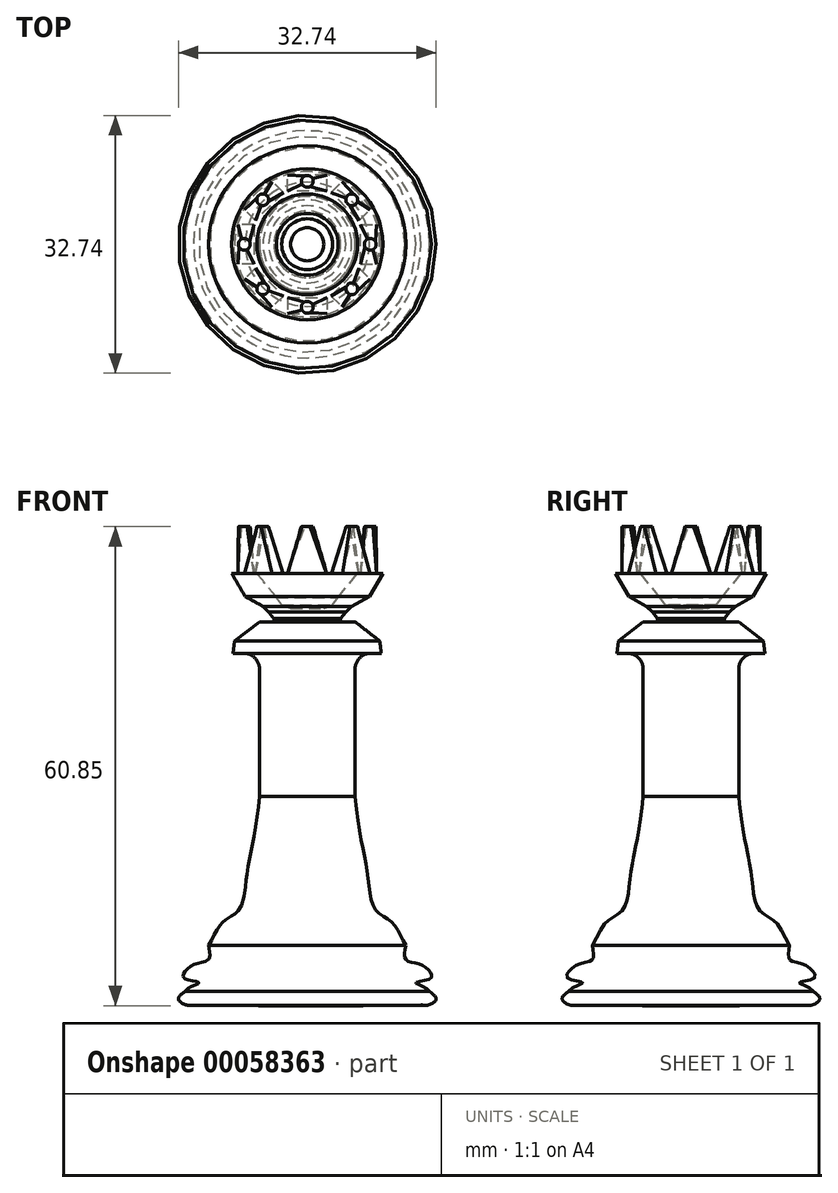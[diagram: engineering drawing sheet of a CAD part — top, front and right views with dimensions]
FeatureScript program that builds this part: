
annotation { "Feature Type Name" : "Feature", "Feature Type Description" : "" }
export const myFeature = defineFeature(function(context is Context, id is Id, definition is map)
    precondition{}
    {
        {
            var Q0;
            Q0=qCreatedBy(makeId("Front.planeOp"),FACE);
            var sketch = newSketch(context, id + "F0", { "sketchPlane" : qUnion([Q0])});
            skLineSegment(sketch, "E0.bottom", {"start": v(0, 26.82) * mm, "end": v(-6.07, 26.82) * mm});
            skLineSegment(sketch, "E0.top", {"start": v(0, -21.95) * mm, "end": v(-6.17, -21.95) * mm});
            skLineSegment(sketch, "E0.left", {"start": v(0, 26.82) * mm, "end": v(0, -21.95) * mm});
            skLineSegment(sketch, "E0.right", {"start": v(-6.07, 26.82) * mm, "end": v(-6.07, 4.6) * mm});
            skLineSegment(sketch, "E1", {"start": v(-6.07, 26.82) * mm, "end": v(-9.2, 24.38) * mm});
            skLineSegment(sketch, "E2", {"start": v(-9.2, 24.38) * mm, "end": v(-9.4, 22.82) * mm});
            skLineSegment(sketch, "E3", {"start": v(-9.4, 22.82) * mm, "end": v(-6.07, 22.82) * mm});
            skLineSegment(sketch, "E4", {"start": v(-6.07, 22.82) * mm, "end": v(-6.07, 26.82) * mm});
            skLineSegment(sketch, "E5", {"start": v(-6.07, -14.27) * mm, "end": v(-6.17, -21.95) * mm});
            skPoint(sketch, "E6.1.internal.snap0", {"position": v(-9.3, -14.27) * mm});
            skPoint(sketch, "E7.1.internal.snap0", {"position": v(-10.85, -21.06) * mm});
            skFitSpline(sketch, "E7", {"points": [v(-12.53, -14.27) * mm, v(-10.85, -11.46) * mm, v(-8.62, -9.7) * mm, v(-7.64, -5) * mm, v(-6.07, 4.6) * mm], "startDerivative": vector(8.85, 12.63) * mm, "endDerivative": vector(3.32, 39) * mm});
            skPoint(sketch, "E8.start.orphan", {"position": v(-15.63, -17.73) * mm});
            skPoint(sketch, "E9.start.orphan", {"position": v(-15.63, -18.5) * mm});
            skPoint(sketch, "E10.orphan", {"position": v(-15.54, -20.16) * mm});
            skFitSpline(sketch, "E11", {"points": [v(-12.53, -14.27) * mm, v(-12.53, -16.09) * mm, v(-14.15, -16.64) * mm, v(-15.63, -17.73) * mm, v(-15.63, -18.5) * mm, v(-13.78, -19.05) * mm, v(-15.54, -20.16) * mm, v(-14.43, -21.36) * mm, v(-12.53, -20.16) * mm, v(-6.17, -21.95) * mm], "startDerivative": vector(4.35, -21.12) * mm, "endDerivative": vector(37.5, -4.8) * mm});
            skLineSegment(sketch, "E12", {"start": v(-6.17, -21.95) * mm, "end": v(-14.43, -21.85) * mm});
            skFitSpline(sketch, "E13", {"points": [v(-14.43, -21.85) * mm, v(-15.44, -21.85) * mm, v(-16.37, -21.08) * mm, v(-15.54, -20.16) * mm], "startDerivative": vector(-3.06, -0.55) * mm, "endDerivative": vector(3.74, 2.62) * mm});
            skSolve(sketch);
        }
        {
            var Q0;
            Q0=qSketchRegion(id+"F0",true);
            var Q1;
            Q1=sQuery(id+"F0.wireOp",EDGE,"E0.left");
            revolve(context, id + "F1", {"entities" : qUnion([Q0]), "axis" : qUnion([Q1]), "revolveType" : RevolveType.FULL});
        }
        {
            var Q0;
            Q0=qCreatedBy(makeId("Front.planeOp"),FACE);
            var sketch = newSketch(context, id + "F2", { "sketchPlane" : qUnion([Q0])});
            skLineSegment(sketch, "E14", {"start": v(0, 26.87) * mm, "end": v(0, 28.51) * mm});
            skLineSegment(sketch, "E15", {"start": v(0, 28.51) * mm, "end": v(-2.1, 28.51) * mm});
            skLineSegment(sketch, "E16", {"start": v(-2.1, 28.51) * mm, "end": v(-3.24, 28.95) * mm});
            skLineSegment(sketch, "E17", {"start": v(-3.24, 28.95) * mm, "end": v(-3.93, 29.92) * mm});
            skLineSegment(sketch, "E18", {"start": v(-3.93, 29.92) * mm, "end": v(-6.4, 32.97) * mm});
            skLineSegment(sketch, "E19", {"start": v(-6.4, 32.97) * mm, "end": v(-9.6, 32.97) * mm});
            skLineSegment(sketch, "E20", {"start": v(-9.6, 32.97) * mm, "end": v(-7.88, 30.03) * mm});
            skLineSegment(sketch, "E21", {"start": v(-7.88, 30.03) * mm, "end": v(-5.64, 28.78) * mm});
            skLineSegment(sketch, "E22", {"start": v(-5.64, 28.78) * mm, "end": v(-4.9, 28.04) * mm});
            skLineSegment(sketch, "E23", {"start": v(-4.9, 28.04) * mm, "end": v(-4.25, 27.2) * mm});
            skLineSegment(sketch, "E24", {"start": v(-4.25, 27.2) * mm, "end": v(-4.25, 26.55) * mm});
            skLineSegment(sketch, "E25", {"start": v(-4.25, 26.55) * mm, "end": v(0, 26.55) * mm});
            skLineSegment(sketch, "E26", {"start": v(0, 26.55) * mm, "end": v(0, 28.51) * mm});
            skSolve(sketch);
        }
        {
            var Q0;
            Q0=qSketchRegion(id+"F2",true);
            var Q1;
            Q1=sQuery(id+"F2.wireOp",EDGE,"E14");
            revolve(context, id + "F3", {"operationType" : NewBodyOperationType.ADD, "entities" : qUnion([Q0]), "axis" : qUnion([Q1]), "revolveType" : RevolveType.FULL});
        }
        {
            var Q0;
            Q0=makeQuery(id+"F1.opRevolve","SWEPT_EDGE",EDGE,{"disambiguationData":[OSD([sQuery(id+"F0.wireOp",EDGE,"E0.right"),sQuery(id+"F0.wireOp",EDGE,"E3"),sQuery(id+"F0.wireOp",EDGE,"E4")])]});
            fillet(context, id + "F4", {"entities" : qUnion([Q0]), "radius" : 2 * mm, "tangentPropagation" : true, "allowEdgeOverflow" : false});
        }
        {
            var Q0;
            Q0=qCreatedBy(makeId("Top.planeOp"),FACE);
            cPlane(context, id + "F5", {"entities" : qUnion([Q0]), "cplaneType" : CPlaneType.OFFSET, "offset" : 32.9 * mm, "width" : 150 * mm, "height" : 150 * mm});
        }
        {
            var Q0;
            Q0=qCreatedBy(id+"F5.planeOp",FACE);
            cPlane(context, id + "F6", {"entities" : qUnion([Q0]), "cplaneType" : CPlaneType.OFFSET, "offset" : 6 * mm, "width" : 150 * mm, "height" : 150 * mm});
        }
        {
            var Q0;
            Q0=qCreatedBy(id+"F5.planeOp",FACE);
            var sketch = newSketch(context, id + "F7", { "sketchPlane" : qUnion([Q0])});
            skLineSegment(sketch, "E27.MirrorCS", {"start": v(2.5, -6.78) * mm, "end": v(2.5, -8.78) * mm});
            skLineSegment(sketch, "E28.MirrorCS", {"start": v(-2.5, -6.78) * mm, "end": v(-2.5, -8.78) * mm});
            skLineSegment(sketch, "E29.MirrorCS", {"start": v(-2.5, -8.78) * mm, "end": v(2.5, -8.78) * mm});
            skLineSegment(sketch, "E30.MirrorCS", {"start": v(-2.5, -6.78) * mm, "end": v(2.5, -6.78) * mm});
            skLineSegment(sketch, "E31", {"start": v(0, 0) * mm, "end": v(0, -8.78) * mm, "construction": true});
            skSolve(sketch);
        }
        {
            var Q0;
            Q0=qCreatedBy(id+"F6.planeOp",FACE);
            var sketch = newSketch(context, id + "F8", { "sketchPlane" : qUnion([Q0])});
            skLineSegment(sketch, "E32", {"start": v(0, 0) * mm, "end": v(0, -8) * mm, "construction": true});
            skCircle(sketch, "E33", {"center": v(0, -8) * mm, "radius": 0.75 * mm});
            skSolve(sketch);
        }
        {
            var Q0;
            Q0=qCreatedBy(id+"F5.planeOp",FACE);
            var sketch = newSketch(context, id + "F9", { "sketchPlane" : qUnion([Q0])});
            skLineSegment(sketch, "E34.bottom", {"start": v(-8.21, 1.63) * mm, "end": v(-7.1, 1.63) * mm});
            skLineSegment(sketch, "E34.top", {"start": v(-8.21, -1.5) * mm, "end": v(-7.1, -1.5) * mm});
            skLineSegment(sketch, "E34.left", {"start": v(-8.21, 1.63) * mm, "end": v(-8.21, -1.5) * mm});
            skLineSegment(sketch, "E34.right", {"start": v(-7.1, 1.63) * mm, "end": v(-7.1, -1.5) * mm});
            skSolve(sketch);
        }
        {
            var Q0;
            Q0=qCreatedBy(id+"F5.planeOp",FACE);
            var sketch = newSketch(context, id + "F10", { "sketchPlane" : qUnion([Q0])});
            skLineSegment(sketch, "E35.bottom", {"start": v(-1.94, 8.39) * mm, "end": v(1.68, 8.39) * mm});
            skLineSegment(sketch, "E35.top", {"start": v(-1.94, 7.22) * mm, "end": v(1.68, 7.22) * mm});
            skLineSegment(sketch, "E35.left", {"start": v(-1.94, 8.39) * mm, "end": v(-1.94, 7.22) * mm});
            skLineSegment(sketch, "E35.right", {"start": v(1.68, 8.39) * mm, "end": v(1.68, 7.22) * mm});
            skSolve(sketch);
        }
        {
            var Q0;
            Q0=qCreatedBy(id+"F5.planeOp",FACE);
            var sketch = newSketch(context, id + "F11", { "sketchPlane" : qUnion([Q0])});
            skLineSegment(sketch, "E36.bottom", {"start": v(7.07, 1.63) * mm, "end": v(8.19, 1.63) * mm});
            skLineSegment(sketch, "E36.top", {"start": v(7.07, -1.46) * mm, "end": v(8.19, -1.46) * mm});
            skLineSegment(sketch, "E36.left", {"start": v(7.07, 1.63) * mm, "end": v(7.07, -1.46) * mm});
            skLineSegment(sketch, "E36.right", {"start": v(8.19, 1.63) * mm, "end": v(8.19, -1.46) * mm});
            skSolve(sketch);
        }
        {
            var Q0;
            Q0=qCreatedBy(id+"F6.planeOp",FACE);
            var sketch = newSketch(context, id + "F12", { "sketchPlane" : qUnion([Q0])});
            skLineSegment(sketch, "E37.bottom", {"start": v(-7.8, 0.25) * mm, "end": v(-7.49, 0.25) * mm});
            skLineSegment(sketch, "E37.top", {"start": v(-7.8, -0.26) * mm, "end": v(-7.49, -0.26) * mm});
            skLineSegment(sketch, "E37.left", {"start": v(-7.8, 0.25) * mm, "end": v(-7.8, -0.26) * mm});
            skLineSegment(sketch, "E37.right", {"start": v(-7.49, 0.25) * mm, "end": v(-7.49, -0.26) * mm});
            skSolve(sketch);
        }
        {
            var Q0;
            Q0=qCreatedBy(id+"F6.planeOp",FACE);
            var sketch = newSketch(context, id + "F13", { "sketchPlane" : qUnion([Q0])});
            skLineSegment(sketch, "E38.bottom", {"start": v(-0.52, 7.92) * mm, "end": v(0.2, 7.92) * mm});
            skLineSegment(sketch, "E38.top", {"start": v(-0.52, 7.64) * mm, "end": v(0.2, 7.64) * mm});
            skLineSegment(sketch, "E38.left", {"start": v(-0.52, 7.92) * mm, "end": v(-0.52, 7.64) * mm});
            skLineSegment(sketch, "E38.right", {"start": v(0.2, 7.92) * mm, "end": v(0.2, 7.64) * mm});
            skSolve(sketch);
        }
        {
            var Q0;
            Q0=qCreatedBy(id+"F6.planeOp",FACE);
            var sketch = newSketch(context, id + "F14", { "sketchPlane" : qUnion([Q0])});
            skLineSegment(sketch, "E39.bottom", {"start": v(7.46, 0.25) * mm, "end": v(7.75, 0.25) * mm});
            skLineSegment(sketch, "E39.top", {"start": v(7.46, -0.26) * mm, "end": v(7.75, -0.26) * mm});
            skLineSegment(sketch, "E39.left", {"start": v(7.46, 0.25) * mm, "end": v(7.46, -0.26) * mm});
            skLineSegment(sketch, "E39.right", {"start": v(7.75, 0.25) * mm, "end": v(7.75, -0.26) * mm});
            skSolve(sketch);
        }
        {
            var Q1;
            Q1 = qSketchRegion(id + "F7", true);
            var Q2;
            Q2 = qSketchRegion(id + "F8", true);
            loft(context, id + "F15", {"sheetProfilesArray" : [{ "sheetProfileEntities" : qUnion([Q1]) }, { "sheetProfileEntities" : qUnion([Q2]) }]});
        }
        {
            var Q0;
            Q0=qCreatedBy(id+"F6.planeOp",FACE);
            var sketch = newSketch(context, id + "F16", { "sketchPlane" : qUnion([Q0])});
            skCircle(sketch, "E40", {"center": v(-7.63, 0) * mm, "radius": 0.53 * mm});
            skCircle(sketch, "E41", {"center": v(0, 8.02) * mm, "radius": 0.51 * mm});
            skCircle(sketch, "E42.MirrorC", {"center": v(7.63, 0) * mm, "radius": 0.53 * mm});
            skFitSpline(sketch, "E43.0", {"points": [v(-0.67, -8.33) * mm, v(-0.63, -8.42) * mm, v(-0.57, -8.5) * mm, v(-0.5, -8.56) * mm, v(-0.42, -8.63) * mm, v(-0.34, -8.68) * mm, v(-0.24, -8.7) * mm, v(-0.15, -8.74) * mm, v(-0.05, -8.75) * mm, v(0.05, -8.75) * mm, v(0.14, -8.74) * mm, v(0.24, -8.72) * mm, v(0.33, -8.67) * mm]});
            skFitSpline(sketch, "E44.0", {"points": [v(0.33, -8.67) * mm, v(0.42, -8.63) * mm, v(0.5, -8.57) * mm, v(0.56, -8.5) * mm, v(0.63, -8.42) * mm, v(0.68, -8.34) * mm, v(0.7, -8.24) * mm, v(0.74, -8.15) * mm, v(0.75, -8.05) * mm, v(0.75, -7.95) * mm, v(0.74, -7.86) * mm, v(0.72, -7.76) * mm, v(0.67, -7.67) * mm]});
            skFitSpline(sketch, "E45.0", {"points": [v(0.67, -7.67) * mm, v(0.63, -7.58) * mm, v(0.57, -7.5) * mm, v(0.5, -7.44) * mm, v(0.42, -7.37) * mm, v(0.34, -7.32) * mm, v(0.24, -7.3) * mm, v(0.15, -7.26) * mm, v(0.05, -7.25) * mm, v(-0.05, -7.25) * mm, v(-0.14, -7.26) * mm, v(-0.24, -7.28) * mm, v(-0.33, -7.33) * mm]});
            skFitSpline(sketch, "E46.0", {"points": [v(-0.33, -7.33) * mm, v(-0.42, -7.37) * mm, v(-0.5, -7.43) * mm, v(-0.56, -7.5) * mm, v(-0.63, -7.58) * mm, v(-0.68, -7.66) * mm, v(-0.7, -7.76) * mm, v(-0.74, -7.85) * mm, v(-0.75, -7.95) * mm, v(-0.75, -8.05) * mm, v(-0.74, -8.14) * mm, v(-0.72, -8.24) * mm, v(-0.67, -8.33) * mm]});
            skSolve(sketch);
        }
        {
            var Q0;
            Q0=qCreatedBy(id+"F5.planeOp",FACE);
            var sketch = newSketch(context, id + "F17", { "sketchPlane" : qUnion([Q0])});
            skLineSegment(sketch, "E47.MirrorCS", {"start": v(-6.5, -3.76) * mm, "end": v(-7.24, -4.12) * mm});
            skLineSegment(sketch, "E48.MirrorCS", {"start": v(-5.17, -6.64) * mm, "end": v(-4.7, -6.1) * mm});
            skLineSegment(sketch, "E49.MirrorCS", {"start": v(-5.8, -5.15) * mm, "end": v(-6.5, -3.76) * mm});
            skLineSegment(sketch, "E50.MirrorCS", {"start": v(-4.7, -6.1) * mm, "end": v(-5.8, -5.15) * mm});
            skLineSegment(sketch, "E51.MirrorCS", {"start": v(-6.47, -5.53) * mm, "end": v(-5.17, -6.64) * mm});
            skLineSegment(sketch, "E52.MirrorCS", {"start": v(-7.24, -4.12) * mm, "end": v(-6.47, -5.53) * mm});
            skSolve(sketch);
        }
        {
            var Q0;
            Q0=qCreatedBy(id+"F5.planeOp",FACE);
            var sketch = newSketch(context, id + "F18", { "sketchPlane" : qUnion([Q0])});
            skLineSegment(sketch, "E53", {"start": v(-7.3, 4.15) * mm, "end": v(-6.4, 5.62) * mm});
            skLineSegment(sketch, "E54", {"start": v(-6.4, 5.62) * mm, "end": v(-5.13, 6.66) * mm});
            skLineSegment(sketch, "E55", {"start": v(-5.13, 6.66) * mm, "end": v(-4.64, 6.06) * mm});
            skLineSegment(sketch, "E56", {"start": v(-4.64, 6.06) * mm, "end": v(-5.82, 5.1) * mm});
            skLineSegment(sketch, "E57", {"start": v(-5.82, 5.1) * mm, "end": v(-6.5, 3.7) * mm});
            skLineSegment(sketch, "E58", {"start": v(-6.5, 3.7) * mm, "end": v(-7.3, 4.15) * mm});
            skSolve(sketch);
        }
        {
            var Q0;
            Q0=qCreatedBy(id+"F5.planeOp",FACE);
            var sketch = newSketch(context, id + "F19", { "sketchPlane" : qUnion([Q0])});
            skLineSegment(sketch, "E59", {"start": v(4.7, 6.06) * mm, "end": v(5.21, 6.68) * mm});
            skLineSegment(sketch, "E60", {"start": v(5.21, 6.68) * mm, "end": v(6.42, 5.56) * mm});
            skLineSegment(sketch, "E61", {"start": v(6.42, 5.56) * mm, "end": v(7.22, 4.09) * mm});
            skLineSegment(sketch, "E62", {"start": v(7.22, 4.09) * mm, "end": v(6.53, 3.72) * mm});
            skLineSegment(sketch, "E63", {"start": v(6.53, 3.72) * mm, "end": v(5.83, 5.15) * mm});
            skLineSegment(sketch, "E64", {"start": v(5.83, 5.15) * mm, "end": v(4.7, 6.06) * mm});
            skSolve(sketch);
        }
        {
            var Q0;
            Q0=qCreatedBy(id+"F5.planeOp",FACE);
            var sketch = newSketch(context, id + "F20", { "sketchPlane" : qUnion([Q0])});
            skLineSegment(sketch, "E65", {"start": v(4.65, -6.09) * mm, "end": v(5.77, -5.17) * mm});
            skLineSegment(sketch, "E66", {"start": v(5.77, -5.17) * mm, "end": v(6.5, -3.73) * mm});
            skLineSegment(sketch, "E67", {"start": v(6.5, -3.73) * mm, "end": v(7.26, -4.11) * mm});
            skLineSegment(sketch, "E68", {"start": v(7.26, -4.11) * mm, "end": v(6.48, -5.63) * mm});
            skLineSegment(sketch, "E69", {"start": v(6.48, -5.63) * mm, "end": v(5.18, -6.65) * mm});
            skLineSegment(sketch, "E70", {"start": v(5.18, -6.65) * mm, "end": v(4.65, -6.09) * mm});
            skSolve(sketch);
        }
        {
            var Q0;
            Q0=qCreatedBy(id+"F6.planeOp",FACE);
            var sketch = newSketch(context, id + "F21", { "sketchPlane" : qUnion([Q0])});
            skLineSegment(sketch, "E71.MirrorCS", {"start": v(-6.25, -4.9) * mm, "end": v(-6.38, -4.96) * mm});
            skLineSegment(sketch, "E72.MirrorCS", {"start": v(-6.12, -5.22) * mm, "end": v(-6.25, -4.9) * mm});
            skLineSegment(sketch, "E73.MirrorCS", {"start": v(-5.87, -5.42) * mm, "end": v(-6.12, -5.22) * mm});
            skLineSegment(sketch, "E74.MirrorCS", {"start": v(-5.95, -5.52) * mm, "end": v(-5.87, -5.42) * mm});
            skLineSegment(sketch, "E75.MirrorCS", {"start": v(-6.24, -5.3) * mm, "end": v(-5.95, -5.52) * mm});
            skLineSegment(sketch, "E76.MirrorCS", {"start": v(-6.38, -4.96) * mm, "end": v(-6.24, -5.3) * mm});
            skSolve(sketch);
        }
        {
            var Q0;
            Q0=qCreatedBy(id+"F6.planeOp",FACE);
            var sketch = newSketch(context, id + "F22", { "sketchPlane" : qUnion([Q0])});
            skLineSegment(sketch, "E77", {"start": v(-6.38, 4.96) * mm, "end": v(-6.24, 5.3) * mm});
            skLineSegment(sketch, "E78", {"start": v(-6.24, 5.3) * mm, "end": v(-5.95, 5.52) * mm});
            skLineSegment(sketch, "E79", {"start": v(-5.95, 5.52) * mm, "end": v(-5.87, 5.41) * mm});
            skLineSegment(sketch, "E80", {"start": v(-5.87, 5.41) * mm, "end": v(-6.12, 5.22) * mm});
            skLineSegment(sketch, "E81", {"start": v(-6.12, 5.22) * mm, "end": v(-6.25, 4.9) * mm});
            skLineSegment(sketch, "E82", {"start": v(-6.25, 4.9) * mm, "end": v(-6.38, 4.96) * mm});
            skSolve(sketch);
        }
        {
            var Q0;
            Q0=qCreatedBy(id+"F6.planeOp",FACE);
            var sketch = newSketch(context, id + "F23", { "sketchPlane" : qUnion([Q0])});
            skLineSegment(sketch, "E83", {"start": v(5.95, 5.52) * mm, "end": v(5.86, 5.41) * mm});
            skLineSegment(sketch, "E84", {"start": v(5.86, 5.41) * mm, "end": v(6.11, 5.22) * mm});
            skLineSegment(sketch, "E85", {"start": v(6.11, 5.22) * mm, "end": v(6.25, 4.9) * mm});
            skLineSegment(sketch, "E86", {"start": v(6.25, 4.9) * mm, "end": v(6.38, 4.96) * mm});
            skLineSegment(sketch, "E87", {"start": v(6.38, 4.96) * mm, "end": v(6.24, 5.3) * mm});
            skLineSegment(sketch, "E88", {"start": v(6.24, 5.3) * mm, "end": v(5.95, 5.52) * mm});
            skSolve(sketch);
        }
        {
            var Q0;
            Q0=qCreatedBy(id+"F6.planeOp",FACE);
            var sketch = newSketch(context, id + "F24", { "sketchPlane" : qUnion([Q0])});
            skLineSegment(sketch, "E89", {"start": v(5.87, -5.41) * mm, "end": v(6.12, -5.22) * mm});
            skLineSegment(sketch, "E90", {"start": v(6.12, -5.22) * mm, "end": v(6.25, -4.9) * mm});
            skLineSegment(sketch, "E91", {"start": v(6.25, -4.9) * mm, "end": v(6.38, -4.96) * mm});
            skLineSegment(sketch, "E92", {"start": v(6.38, -4.96) * mm, "end": v(6.24, -5.3) * mm});
            skLineSegment(sketch, "E93", {"start": v(6.24, -5.3) * mm, "end": v(5.95, -5.52) * mm});
            skLineSegment(sketch, "E94", {"start": v(5.95, -5.52) * mm, "end": v(5.87, -5.42) * mm});
            skSolve(sketch);
        }
        {
            var Q0;
            Q0=qCreatedBy(id+"F6.planeOp",FACE);
            var sketch = newSketch(context, id + "F25", { "sketchPlane" : qUnion([Q0])});
            skCircle(sketch, "E95", {"center": v(-6.18, 5.22) * mm, "radius": 0.5 * mm});
            skCircle(sketch, "E96.MirrorC", {"center": v(6.18, 5.22) * mm, "radius": 0.5 * mm});
            skCircle(sketch, "E97.MirrorC", {"center": v(-6.18, -5.22) * mm, "radius": 0.5 * mm});
            skCircle(sketch, "E98.MirrorC", {"center": v(6.18, -5.22) * mm, "radius": 0.5 * mm});
            skSolve(sketch);
        }
        {
            var Q0;
            Q0=makeQuery(id+"F15.opLoft","SWEPT_BODY",BODY,{"disambiguationData":[OSD([makeQuery(id+"F7.imprint","IMPRINT",FACE,{"disambiguationData":[TD([[makeQuery(id+"F7.imprint","IMPRINT",EDGE,{"derivedFrom":sQuery(id+"F7.wireOp",EDGE,"E27.MirrorCS")}),-1.0]])]}),makeQuery(id+"F8.imprint","IMPRINT",FACE,{"disambiguationData":[TD([[makeQuery(id+"F8.imprint","IMPRINT",EDGE,{"derivedFrom":sQuery(id+"F8.wireOp",EDGE,"E33")}),1.0]])]})])]});
            var Q1;
            Q1=makeQuery(id+"F3.opRevolve","SWEPT_EDGE",EDGE,{"disambiguationData":[OSD([sQuery(id+"F2.wireOp",EDGE,"E18"),sQuery(id+"F2.wireOp",EDGE,"E19")])]});
            circularPattern(context, id + "F26", {"entities" : qUnion([Q0]), "axis" : qUnion([Q1]), "angle" : 360 * degree, "instanceCount" : 8, "equalSpace" : true});
        }
    });
